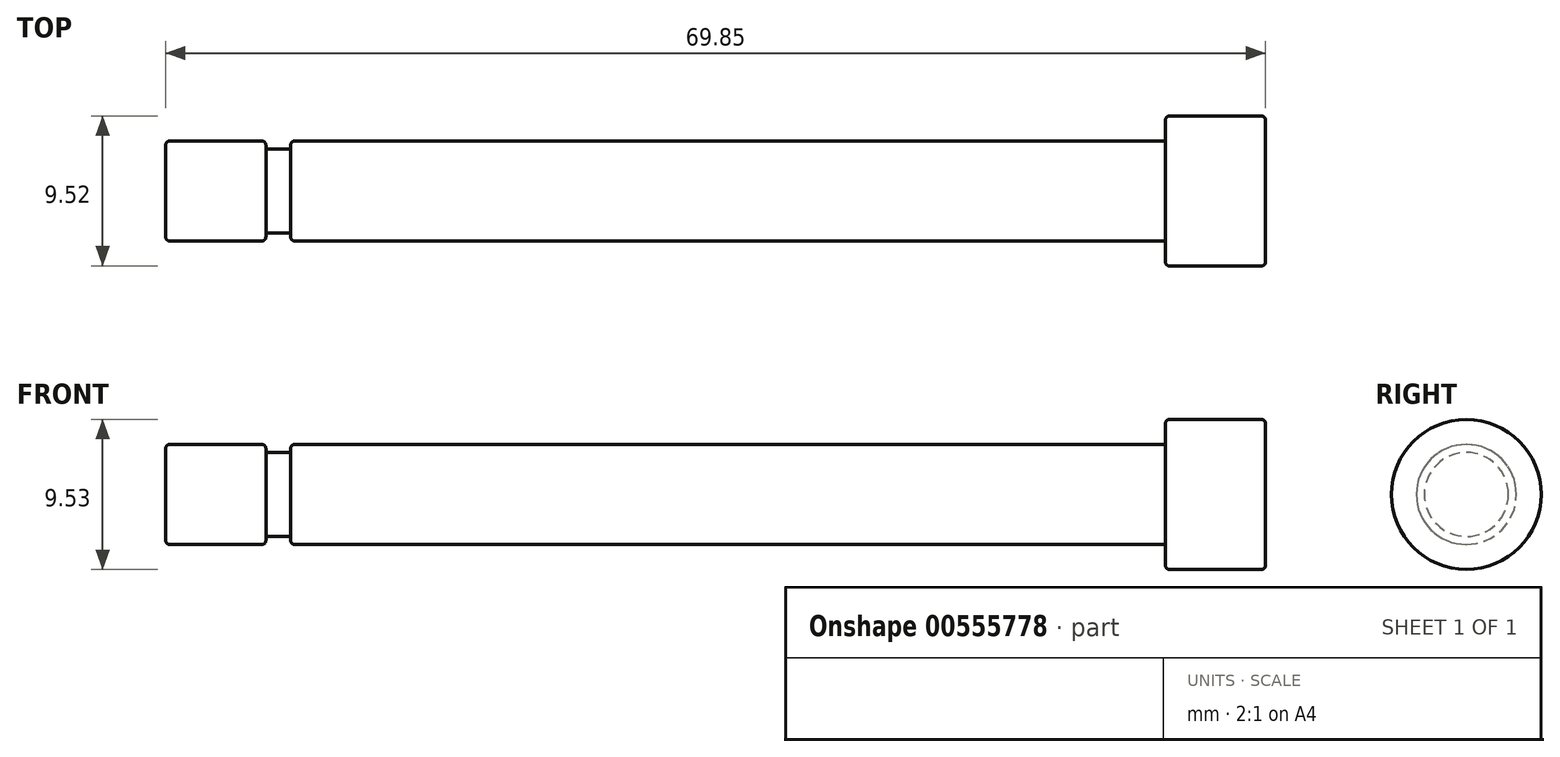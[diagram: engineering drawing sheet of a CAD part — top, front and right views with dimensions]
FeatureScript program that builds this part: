
annotation { "Feature Type Name" : "Feature", "Feature Type Description" : "" }
export const myFeature = defineFeature(function(context is Context, id is Id, definition is map)
    precondition{}
    {
        {
            var Q0;
            Q0=qCreatedBy(makeId("Front.planeOp"),FACE);
            var sketch = newSketch(context, id + "F0", { "sketchPlane" : qUnion([Q0])});
            skLineSegment(sketch, "E0", {"start": v(0, 0) * mm, "end": v(6.36, 0) * mm});
            skLineSegment(sketch, "E1", {"start": v(6.36, 0) * mm, "end": v(6.36, -0.5) * mm});
            skLineSegment(sketch, "E2", {"start": v(6.36, -0.5) * mm, "end": v(7.94, -0.5) * mm});
            skLineSegment(sketch, "E3", {"start": v(7.94, -0.5) * mm, "end": v(7.94, 0) * mm});
            skLineSegment(sketch, "E4", {"start": v(7.94, 0) * mm, "end": v(63.5, 0) * mm});
            skLineSegment(sketch, "E5", {"start": v(63.5, 0) * mm, "end": v(63.5, 1.59) * mm});
            skLineSegment(sketch, "E6", {"start": v(63.5, 1.59) * mm, "end": v(69.85, 1.59) * mm});
            skLineSegment(sketch, "E7", {"start": v(69.85, 1.59) * mm, "end": v(69.85, -3.17) * mm});
            skLineSegment(sketch, "E8", {"start": v(69.85, -3.18) * mm, "end": v(0, -3.18) * mm});
            skLineSegment(sketch, "E9", {"start": v(0, -3.17) * mm, "end": v(0, 0) * mm});
            skSolve(sketch);
        }
        {
            var Q0;
            Q0=makeQuery(id+"F0.imprint","IMPRINT",FACE,{"disambiguationData":[TD([[makeQuery(id+"F0.imprint","IMPRINT",EDGE,{"derivedFrom":sQuery(id+"F0.wireOp",EDGE,"E0")}),-1.0]])]});
            var Q1;
            Q1=sQuery(id+"F0.wireOp",EDGE,"E8");
            revolve(context, id + "F1", {"entities" : qUnion([Q0]), "axis" : qUnion([Q1]), "revolveType" : RevolveType.FULL});
        }
        {
            var Q0;
            Q0=makeQuery(id+"F1.opRevolve","SWEPT_EDGE",EDGE,{"disambiguationData":[OSD([sQuery(id+"F0.wireOp",EDGE,"E0"),sQuery(id+"F0.wireOp",EDGE,"E9")])]});
            var Q1;
            Q1=makeQuery(id+"F1.opRevolve","SWEPT_EDGE",EDGE,{"disambiguationData":[OSD([sQuery(id+"F0.wireOp",EDGE,"E5"),sQuery(id+"F0.wireOp",EDGE,"E6")])]});
            var Q2;
            Q2=makeQuery(id+"F1.opRevolve","SWEPT_EDGE",EDGE,{"disambiguationData":[OSD([sQuery(id+"F0.wireOp",EDGE,"E6"),sQuery(id+"F0.wireOp",EDGE,"E7")])]});
            fillet(context, id + "F2", {"entities" : qUnion([Q0, Q1, Q2]), "radius" : 0.25 * mm, "tangentPropagation" : true, "allowEdgeOverflow" : false});
        }
        {
            var Q0;
            Q0=makeQuery(id+"F1.opRevolve","SWEPT_EDGE",EDGE,{"disambiguationData":[OSD([sQuery(id+"F0.wireOp",EDGE,"E3"),sQuery(id+"F0.wireOp",EDGE,"E4")])]});
            var Q1;
            Q1=makeQuery(id+"F1.opRevolve","SWEPT_EDGE",EDGE,{"disambiguationData":[OSD([sQuery(id+"F0.wireOp",EDGE,"E0"),sQuery(id+"F0.wireOp",EDGE,"E1")])]});
            fillet(context, id + "F3", {"entities" : qUnion([Q0, Q1]), "radius" : 0.25 * mm, "tangentPropagation" : true, "allowEdgeOverflow" : false});
        }
    });
